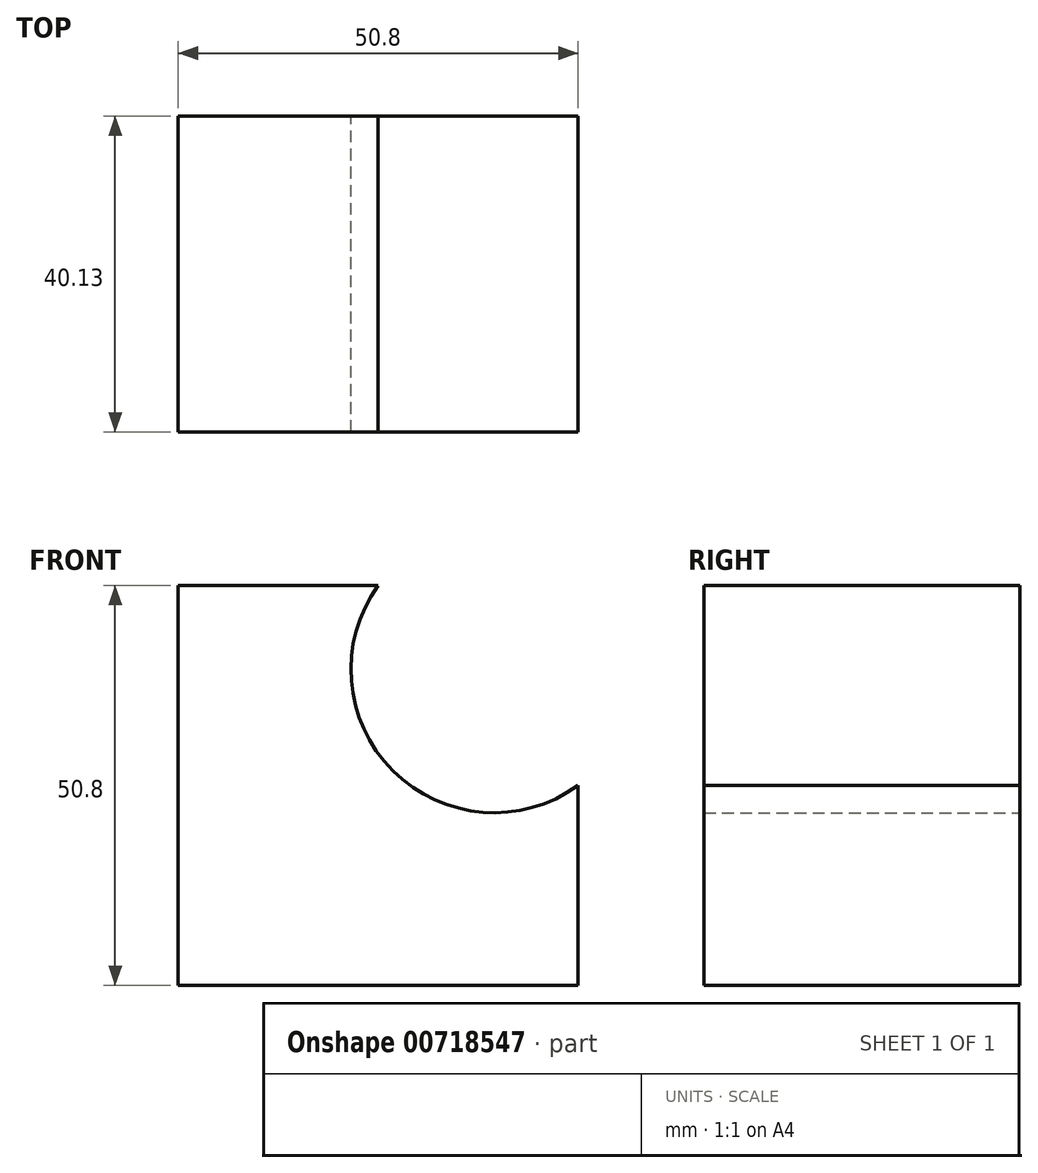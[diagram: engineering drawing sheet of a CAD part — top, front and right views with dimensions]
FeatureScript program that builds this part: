
annotation { "Feature Type Name" : "Feature", "Feature Type Description" : "" }
export const myFeature = defineFeature(function(context is Context, id is Id, definition is map)
    precondition{}
    {
        {
            var Q0;
            Q0=qCreatedBy(makeId("Front.planeOp"),FACE);
            var sketch = newSketch(context, id + "F0", { "sketchPlane" : qUnion([Q0])});
            skLineSegment(sketch, "E0", {"start": v(1.16, 50.8) * mm, "end": v(-24.24, 50.8) * mm});
            skLineSegment(sketch, "E1", {"start": v(-24.24, 50.8) * mm, "end": v(-24.24, 0) * mm});
            skLineSegment(sketch, "E2", {"start": v(-24.24, 0) * mm, "end": v(26.56, 0) * mm});
            skLineSegment(sketch, "E3", {"start": v(26.56, 0) * mm, "end": v(26.56, 25.4) * mm});
            skArc(sketch, "E4", {"start": v(1.16, 50.8) * mm, "mid": v(3.03, 27.27) * mm, "end": v(26.56, 25.4) * mm});
            skSolve(sketch);
        }
        {
            var Q0;
            Q0 = qSketchRegion(id + "F0", true);
            extrude(context, id + "F1", {"entities" : qUnion([Q0]), "depth" : 40.13 * mm, "offsetDistance" : 25.4 * mm});
        }
    });
